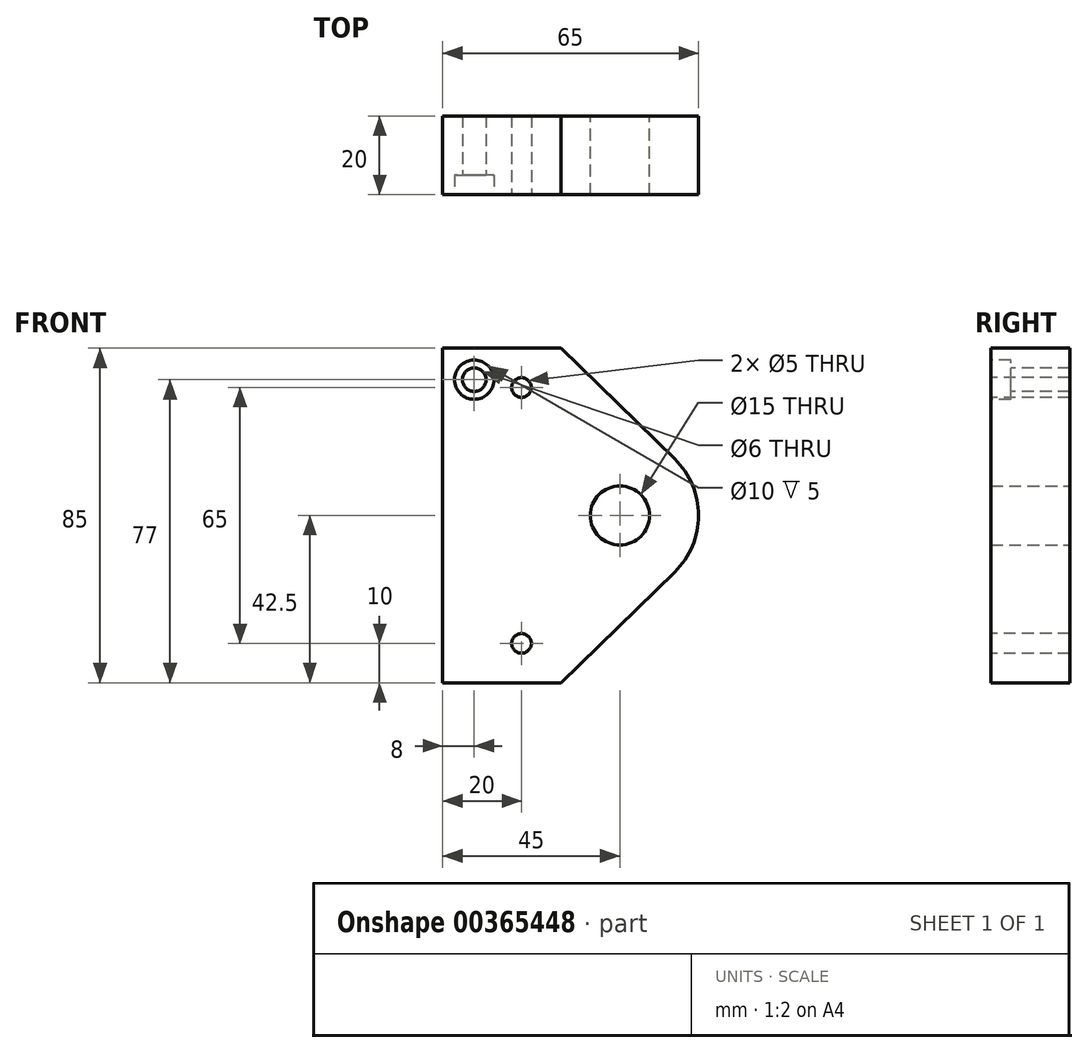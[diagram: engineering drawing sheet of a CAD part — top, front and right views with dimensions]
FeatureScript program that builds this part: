
annotation { "Feature Type Name" : "Feature", "Feature Type Description" : "" }
export const myFeature = defineFeature(function(context is Context, id is Id, definition is map)
    precondition{}
    {
        {
            var Q0;
            Q0=qCreatedBy(makeId("Front.planeOp"),FACE);
            var sketch = newSketch(context, id + "F0", { "sketchPlane" : qUnion([Q0])});
            skLineSegment(sketch, "E0", {"start": v(71.62, 0) * mm, "end": v(-70.91, 0) * mm, "construction": true});
            skLineSegment(sketch, "E1.bottom", {"start": v(-30, 42.5) * mm, "end": v(0, 42.5) * mm});
            skLineSegment(sketch, "E1.top", {"start": v(-30, -42.5) * mm, "end": v(0, -42.5) * mm});
            skLineSegment(sketch, "E1.left", {"start": v(-30, 42.5) * mm, "end": v(-30, -42.5) * mm});
            skArc(sketch, "E2", {"start": v(28.95, -14.33) * mm, "mid": v(35, 0) * mm, "end": v(28.95, 14.33) * mm});
            skLineSegment(sketch, "E3", {"start": v(0, 42.5) * mm, "end": v(28.95, 14.33) * mm});
            skLineSegment(sketch, "E4", {"start": v(0, -42.5) * mm, "end": v(28.95, -14.33) * mm});
            skCircle(sketch, "E5", {"center": v(15, 0) * mm, "radius": 7.5 * mm});
            skSolve(sketch);
        }
        {
            var Q0;
            Q0 = qSketchRegion(id + "F0", true);
            extrude(context, id + "F1", {"entities" : qUnion([Q0]), "depth" : 20 * mm});
        }
        {
            var Q0;
            Q0=makeQuery(id+"F1.opExtrude","CAP_FACE",FACE,{"disambiguationData":[OSD([sQuery(id+"F0.wireOp",EDGE,"E1.bottom"),sQuery(id+"F0.wireOp",EDGE,"E1.top"),sQuery(id+"F0.wireOp",EDGE,"E1.left"),sQuery(id+"F0.wireOp",EDGE,"E2"),sQuery(id+"F0.wireOp",EDGE,"E3"),sQuery(id+"F0.wireOp",EDGE,"E4"),sQuery(id+"F0.wireOp",EDGE,"E5")])],"isStart":false});
            var sketch = newSketch(context, id + "F2", { "sketchPlane" : qUnion([Q0])});
            skLineSegment(sketch, "E6", {"start": v(-10, 42.5) * mm, "end": v(-10, -42.5) * mm, "construction": true});
            skLineSegment(sketch, "E7", {"start": v(-20, 42.5) * mm, "end": v(-20, -42.5) * mm, "construction": true});
            skLineSegment(sketch, "E8.0.0", {"start": v(-30, 42.5) * mm, "end": v(-30, -42.5) * mm});
            skLineSegment(sketch, "E8.0.2", {"start": v(-30, -42.5) * mm, "end": v(-30, 42.5) * mm});
            skCircle(sketch, "E9", {"center": v(-10, 32.5) * mm, "radius": 2.5 * mm});
            skCircle(sketch, "E10", {"center": v(-10, -32.5) * mm, "radius": 2.5 * mm});
            skSolve(sketch);
        }
        {
            var Q0;
            Q0 = qSketchRegion(id + "F2", true);
            extrude(context, id + "F3", {"entities" : qUnion([Q0]), "operationType" : NewBodyOperationType.REMOVE, "endBound" : BoundingType.UP_TO_NEXT, "oppositeDirection" : true, "depth" : 25 * mm});
        }
        {
            var Q0;
            Q0=makeQuery(id+"F1.opExtrude","CAP_FACE",FACE,{"disambiguationData":[OSD([sQuery(id+"F0.wireOp",EDGE,"E1.bottom"),sQuery(id+"F0.wireOp",EDGE,"E1.top"),sQuery(id+"F0.wireOp",EDGE,"E1.left"),sQuery(id+"F0.wireOp",EDGE,"E2"),sQuery(id+"F0.wireOp",EDGE,"E3"),sQuery(id+"F0.wireOp",EDGE,"E4"),sQuery(id+"F0.wireOp",EDGE,"E5")])],"isStart":false});
            var sketch = newSketch(context, id + "F4", { "sketchPlane" : qUnion([Q0])});
            skLineSegment(sketch, "E11.0", {"start": v(-30, 42.5) * mm, "end": v(-30, -42.5) * mm});
            skLineSegment(sketch, "E12.0", {"start": v(-30, 42.5) * mm, "end": v(0, 42.5) * mm});
            skPoint(sketch, "E13", {"position": v(-22, 34.5) * mm});
            skSolve(sketch);
        }
        {
            var Q0;
            Q0=sQuery(id+"F4.wireOp",VERTEX,"E13");
            var Q1;
            Q1=makeQuery(id+"F1.opExtrude","SWEPT_BODY",BODY,{"disambiguationData":[OSD([sQuery(id+"F0.wireOp",EDGE,"E1.bottom"),sQuery(id+"F0.wireOp",EDGE,"E1.top"),sQuery(id+"F0.wireOp",EDGE,"E1.left"),sQuery(id+"F0.wireOp",EDGE,"E2"),sQuery(id+"F0.wireOp",EDGE,"E3"),sQuery(id+"F0.wireOp",EDGE,"E4"),sQuery(id+"F0.wireOp",EDGE,"E5")])]});
            hole(context, id + "F5", {"style" : HoleStyle.C_BORE, "endStyle" : HoleEndStyle.BLIND, "holeDiameter" : 6 * mm, "cBoreDiameter" : 10 * mm, "cBoreDepth" : 5 * mm, "holeDepth" : 20 * mm, "isTappedThrough" : true, "tappedDepth" : 12 * mm, "tapClearance" : 3, "locations" : qUnion([Q0]), "scope" : qUnion([Q1])});
        }
    });
